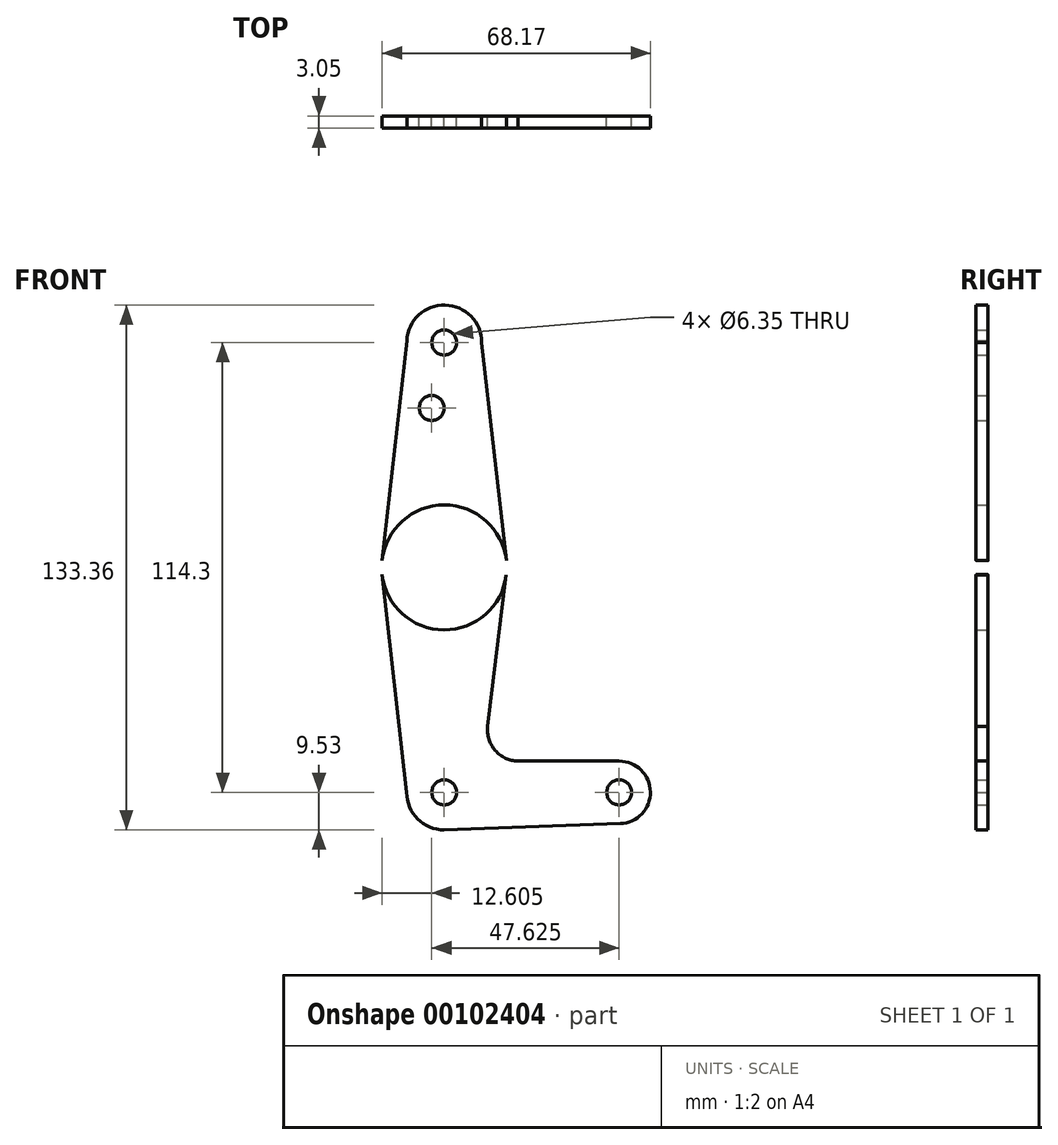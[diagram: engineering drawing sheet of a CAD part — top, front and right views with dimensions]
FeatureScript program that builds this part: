
annotation { "Feature Type Name" : "Feature", "Feature Type Description" : "" }
export const myFeature = defineFeature(function(context is Context, id is Id, definition is map)
    precondition{}
    {
        {
            var Q0;
            Q0=qCreatedBy(makeId("Front.planeOp"),FACE);
            var sketch = newSketch(context, id + "F0", { "sketchPlane" : qUnion([Q0])});
            skLineSegment(sketch, "E0", {"start": v(0, 114.3) * mm, "end": v(0, 0) * mm});
            skLineSegment(sketch, "E1", {"start": v(0, 0) * mm, "end": v(44.45, 0) * mm});
            skCircle(sketch, "E2", {"center": v(0, 114.3) * mm, "radius": 9.53 * mm});
            skCircle(sketch, "E3", {"center": v(44.45, 0) * mm, "radius": 7.94 * mm});
            skCircle(sketch, "E4", {"center": v(0, 57.15) * mm, "radius": 15.88 * mm});
            skLineSegment(sketch, "E5", {"start": v(-9.51, 114.8) * mm, "end": v(-15.78, 58.92) * mm});
            skLineSegment(sketch, "E6", {"start": v(9.52, 114.34) * mm, "end": v(15.77, 58.93) * mm});
            skLineSegment(sketch, "E7", {"start": v(0, -9.53) * mm, "end": v(44.73, -7.93) * mm});
            skLineSegment(sketch, "E8", {"start": v(44.45, 7.94) * mm, "end": v(18.74, 7.94) * mm});
            skArc(sketch, "E9", {"start": v(11.05, 16.77) * mm, "mid": v(12.95, 10.66) * mm, "end": v(18.74, 7.94) * mm});
            skLineSegment(sketch, "E10", {"start": v(-9.52, 0) * mm, "end": v(-15.78, 55.38) * mm});
            skLineSegment(sketch, "E11", {"start": v(11.05, 16.77) * mm, "end": v(15.76, 55.22) * mm});
            skCircle(sketch, "E12", {"center": v(0, 114.3) * mm, "radius": 3.18 * mm});
            skCircle(sketch, "E13", {"center": v(-3.17, 97.66) * mm, "radius": 3.18 * mm});
            skCircle(sketch, "E14", {"center": v(0, 57.15) * mm, "radius": 3.18 * mm});
            skCircle(sketch, "E15", {"center": v(44.45, 0) * mm, "radius": 3.18 * mm});
            skCircle(sketch, "E16", {"center": v(0, 0) * mm, "radius": 3.18 * mm});
            skCircle(sketch, "E17", {"center": v(0, 0) * mm, "radius": 9.53 * mm});
            skSolve(sketch);
        }
        {
            var Q0;
            {var subQ0=sQuery(id+"F0.wireOp",EDGE,"E17");var subQ5=sQuery(id+"F0.wireOp",EDGE,"E0");var subQ6=makeQuery(id+"F0.imprint","INTERSECT",VERTEX,{"derivedFrom":[subQ5,subQ0]});Q0=makeQuery(id+"F0.imprint","IMPRINT",FACE,{"disambiguationData":[TD([[makeQuery(id+"F0.imprint","IMPRINT",EDGE,{"disambiguationData":[TD([[subQ6,-1.0]])],"derivedFrom":subQ5}),-1.0]])]});}
            var Q1;
            {var subQ0=sQuery(id+"F0.wireOp",EDGE,"E17");var subQ1=sQuery(id+"F0.wireOp",EDGE,"E0");var subQ2=makeQuery(id+"F0.imprint","INTERSECT",VERTEX,{"derivedFrom":[subQ1,subQ0]});Q1=makeQuery(id+"F0.imprint","IMPRINT",FACE,{"disambiguationData":[TD([[makeQuery(id+"F0.imprint","IMPRINT",EDGE,{"disambiguationData":[TD([[subQ2,-1.0]])],"derivedFrom":subQ1}),1.0]])]});}
            var Q2;
            {var subQ0=sQuery(id+"F0.wireOp",EDGE,"E8");Q2=makeQuery(id+"F0.imprint","IMPRINT",FACE,{"disambiguationData":[TD([[makeQuery(id+"F0.imprint","IMPRINT",EDGE,{"derivedFrom":subQ0}),1.0]])]});}
            var Q3;
            {var subQ5=sQuery(id+"F0.wireOp",EDGE,"E10");Q3=makeQuery(id+"F0.imprint","IMPRINT",FACE,{"disambiguationData":[TD([[makeQuery(id+"F0.imprint","IMPRINT",EDGE,{"derivedFrom":subQ5}),-1.0]])]});}
            var Q4;
            {var subQ0=sQuery(id+"F0.wireOp",EDGE,"E3");var subQ1=sQuery(id+"F0.wireOp",EDGE,"E1");var subQ2=makeQuery(id+"F0.imprint","INTERSECT",VERTEX,{"derivedFrom":[subQ1,subQ0]});Q4=makeQuery(id+"F0.imprint","IMPRINT",FACE,{"disambiguationData":[TD([[makeQuery(id+"F0.imprint","IMPRINT",EDGE,{"disambiguationData":[TD([[subQ2,1.0]])],"derivedFrom":subQ1}),-1.0]])]});}
            var Q5;
            Q5=makeQuery(id+"F0.imprint","IMPRINT",FACE,{"disambiguationData":[TD([[makeQuery(id+"F0.imprint","IMPRINT",EDGE,{"derivedFrom":sQuery(id+"F0.wireOp",EDGE,"E15")}),-1.0]])]});
            var Q6;
            {var subQ0=sQuery(id+"F0.wireOp",EDGE,"E4");var subQ2=sQuery(id+"F0.wireOp",EDGE,"E0");var subQ7=makeQuery(id+"F0.imprint","INTERSECT",VERTEX,{"disambiguationData":[OD(0.0)],"derivedFrom":[subQ2,subQ0]});Q6=makeQuery(id+"F0.imprint","IMPRINT",FACE,{"disambiguationData":[TD([[makeQuery(id+"F0.imprint","IMPRINT",EDGE,{"disambiguationData":[TD([[subQ7,-1.0]])],"derivedFrom":subQ2}),1.0]])]});}
            var Q7;
            {var subQ0=sQuery(id+"F0.wireOp",EDGE,"E5");Q7=makeQuery(id+"F0.imprint","IMPRINT",FACE,{"disambiguationData":[TD([[makeQuery(id+"F0.imprint","IMPRINT",EDGE,{"derivedFrom":subQ0}),1.0]])]});}
            var Q8;
            {var subQ0=sQuery(id+"F0.wireOp",EDGE,"E6");Q8=makeQuery(id+"F0.imprint","IMPRINT",FACE,{"disambiguationData":[TD([[makeQuery(id+"F0.imprint","IMPRINT",EDGE,{"derivedFrom":subQ0}),-1.0]])]});}
            var Q9;
            Q9=makeQuery(id+"F0.imprint","IMPRINT",FACE,{"disambiguationData":[TD([[makeQuery(id+"F0.imprint","IMPRINT",EDGE,{"derivedFrom":sQuery(id+"F0.wireOp",EDGE,"E12")}),-1.0]])]});
            var Q10;
            {var subQ0=sQuery(id+"F0.wireOp",EDGE,"E4");var subQ4=sQuery(id+"F0.wireOp",EDGE,"E0");var subQ7=makeQuery(id+"F0.imprint","INTERSECT",VERTEX,{"disambiguationData":[OD(0.0)],"derivedFrom":[subQ4,subQ0]});Q10=makeQuery(id+"F0.imprint","IMPRINT",FACE,{"disambiguationData":[TD([[makeQuery(id+"F0.imprint","IMPRINT",EDGE,{"disambiguationData":[TD([[subQ7,-1.0]])],"derivedFrom":subQ4}),-1.0]])]});}
            extrude(context, id + "F1", {"entities" : qUnion([Q0, Q1, Q2, Q3, Q4, Q5, Q6, Q7, Q8, Q9, Q10]), "depth" : 3.05 * mm});
        }
    });
